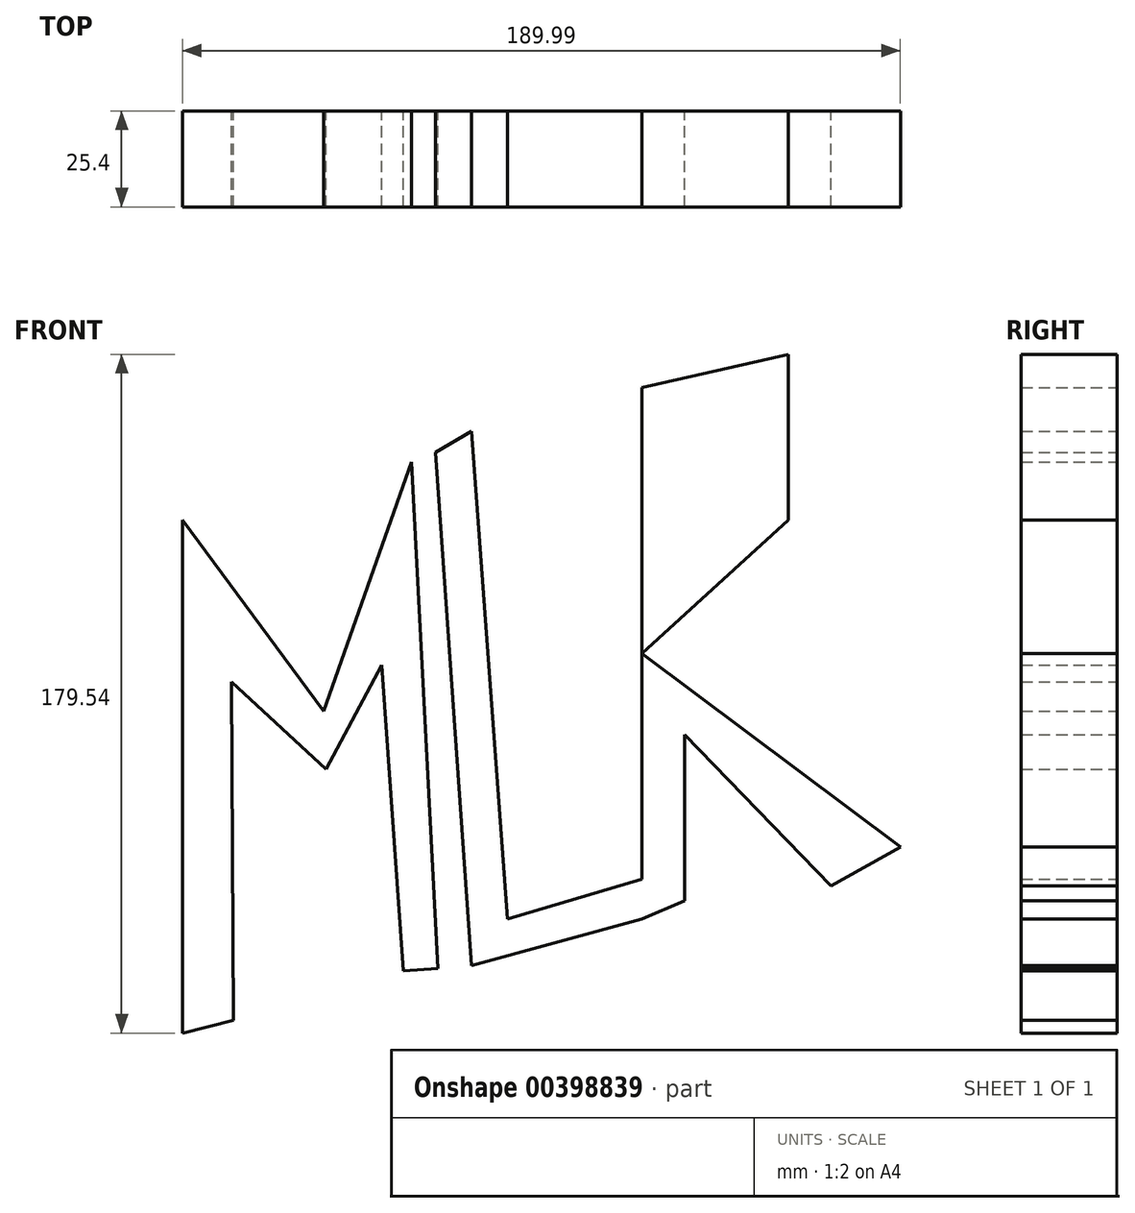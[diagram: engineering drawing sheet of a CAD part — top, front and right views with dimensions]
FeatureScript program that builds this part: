
annotation { "Feature Type Name" : "Feature", "Feature Type Description" : "" }
export const myFeature = defineFeature(function(context is Context, id is Id, definition is map)
    precondition{}
    {
        {
            var Q0;
            Q0=qCreatedBy(makeId("Front.planeOp"),FACE);
            var sketch = newSketch(context, id + "F0", { "sketchPlane" : qUnion([Q0])});
            skLineSegment(sketch, "E0", {"start": v(-45.47, 38.34) * mm, "end": v(-45.47, -97.37) * mm});
            skLineSegment(sketch, "E1", {"start": v(-45.47, 38.34) * mm, "end": v(-8.1, -12.21) * mm});
            skLineSegment(sketch, "E2", {"start": v(-8.1, -12.21) * mm, "end": v(15.16, 53.72) * mm});
            skLineSegment(sketch, "E3", {"start": v(15.16, 53.72) * mm, "end": v(22.2, -80.3) * mm});
            skLineSegment(sketch, "E4", {"start": v(22.2, -80.3) * mm, "end": v(21.5, 56.26) * mm});
            skLineSegment(sketch, "E5", {"start": v(21.5, 56.26) * mm, "end": v(31.02, -79.52) * mm});
            skLineSegment(sketch, "E6", {"start": v(31.02, -79.52) * mm, "end": v(76.14, -67.2) * mm});
            skLineSegment(sketch, "E7", {"start": v(76.14, -67.2) * mm, "end": v(76.14, 73.39) * mm});
            skLineSegment(sketch, "E8", {"start": v(76.14, 73.39) * mm, "end": v(114.91, 82.17) * mm});
            skLineSegment(sketch, "E9", {"start": v(114.91, 82.17) * mm, "end": v(114.91, 38.34) * mm});
            skLineSegment(sketch, "E10", {"start": v(114.91, 38.34) * mm, "end": v(76.14, 3.1) * mm});
            skLineSegment(sketch, "E11", {"start": v(76.14, 3.1) * mm, "end": v(144.52, -48.17) * mm});
            skLineSegment(sketch, "E12", {"start": v(144.52, -48.17) * mm, "end": v(126.2, -58.4) * mm});
            skLineSegment(sketch, "E13", {"start": v(126.2, -58.4) * mm, "end": v(87.42, -18.47) * mm});
            skLineSegment(sketch, "E14", {"start": v(87.42, -18.47) * mm, "end": v(87.42, -62.33) * mm});
            skLineSegment(sketch, "E15", {"start": v(87.42, -62.33) * mm, "end": v(76.14, -67.2) * mm});
            skLineSegment(sketch, "E16", {"start": v(76.14, -56.68) * mm, "end": v(40.54, -67.2) * mm});
            skLineSegment(sketch, "E17", {"start": v(40.54, -67.2) * mm, "end": v(31.02, 61.88) * mm});
            skLineSegment(sketch, "E18", {"start": v(31.02, 61.88) * mm, "end": v(21.5, 56.26) * mm});
            skLineSegment(sketch, "E19", {"start": v(22.2, -80.3) * mm, "end": v(12.98, -80.95) * mm});
            skLineSegment(sketch, "E20", {"start": v(12.98, -80.95) * mm, "end": v(7.3, 0) * mm});
            skLineSegment(sketch, "E21", {"start": v(7.3, 0) * mm, "end": v(-7.4, -27.52) * mm});
            skLineSegment(sketch, "E22", {"start": v(-7.4, -27.52) * mm, "end": v(-32.43, -4.43) * mm});
            skLineSegment(sketch, "E23", {"start": v(-32.43, -4.43) * mm, "end": v(-31.97, -94) * mm});
            skLineSegment(sketch, "E24", {"start": v(-31.97, -94) * mm, "end": v(-45.47, -97.37) * mm});
            skSolve(sketch);
        }
        {
            var Q0;
            Q0 = qSketchRegion(id + "F0", true);
            extrude(context, id + "F1", {"entities" : qUnion([Q0]), "depth" : 25.4 * mm});
        }
    });
